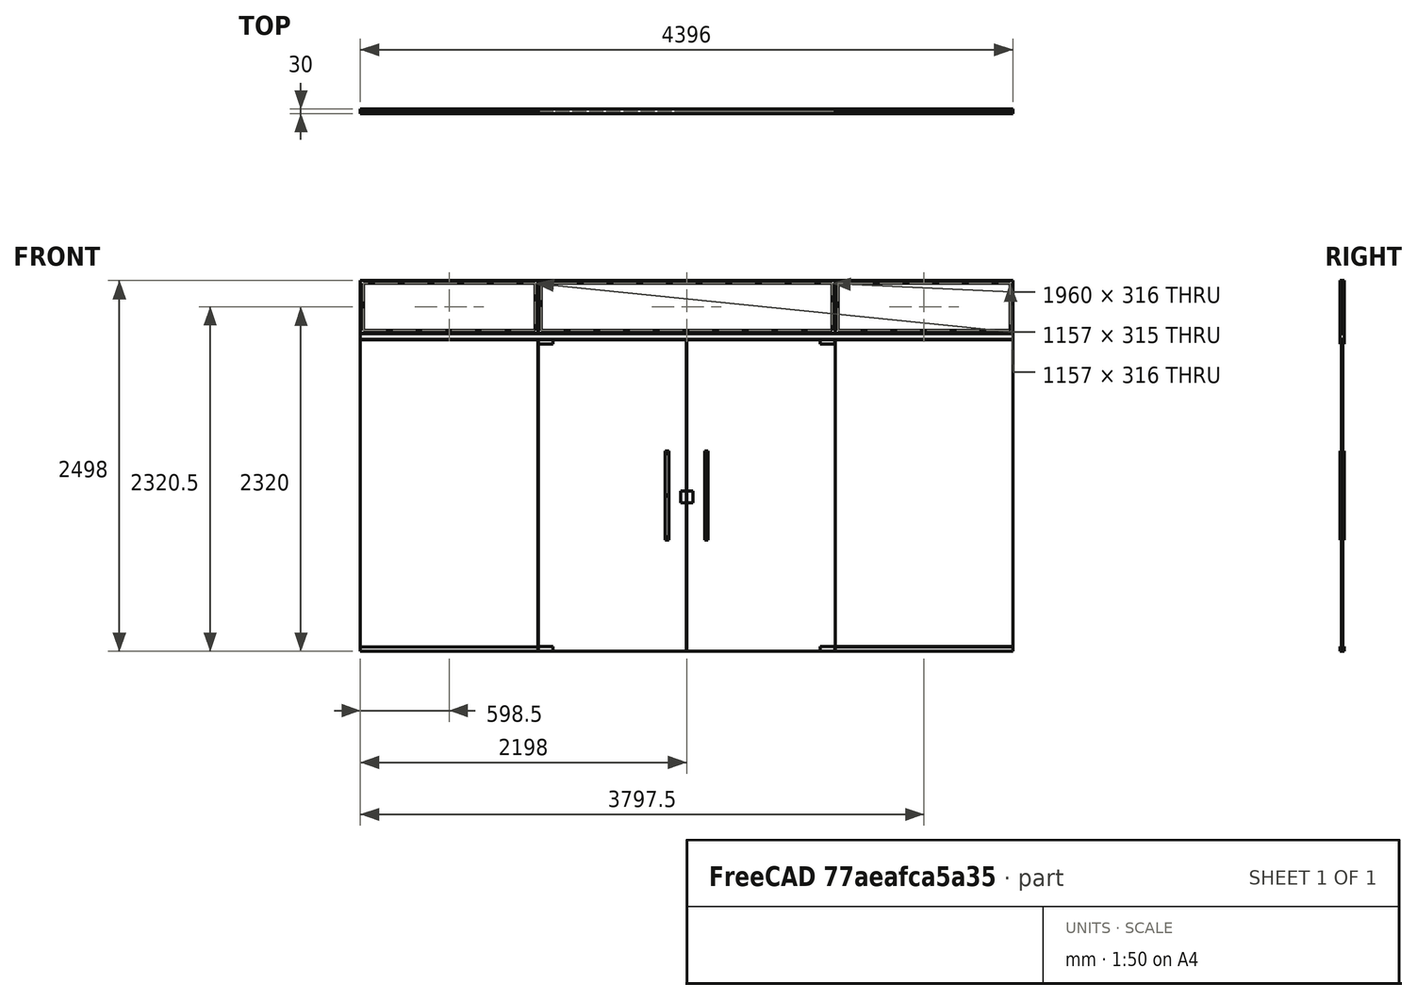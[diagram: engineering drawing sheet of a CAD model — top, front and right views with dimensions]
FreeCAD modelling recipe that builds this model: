
FCSTD DOCUMENT  (FreeCAD 0.16R6704 (Git))
Label: Glass double doors with transom and handles
License: CreativeCommons Attribution
LicenseURL: http://creativecommons.org/licenses/by/4.0/
objects: Sketcher::SketchObject×3, Part::FeaturePython×1, App::DocumentObjectGroup×1
note: 4 computed .brp shape members not serialized (recipe doc carries the construction recipe); baked Part::Feature solids carry a one-line shape summary decoded from their .brp

FEATURE [Sketcher::SketchObject] Sketch138
  Placement = pos=(0,0,0) rot=(1,0,0;1.5708rad)
  sketch-geometry (103):
    g0: LineSegment StartX=1 StartY=0 StartZ=0 EndX=4399 EndY=0 EndZ=0
    g1: LineSegment StartX=4399 StartY=0 StartZ=0 EndX=4399 EndY=2499 EndZ=0
    g2: LineSegment StartX=4399 StartY=2499 StartZ=0 EndX=1 EndY=2499 EndZ=0
    g3: LineSegment StartX=1 StartY=2499 StartZ=0 EndX=1 EndY=0 EndZ=0
    g4: LineSegment StartX=1200 StartY=0 StartZ=0 EndX=2199.5 EndY=0 EndZ=0
    g5: LineSegment StartX=2199.5 StartY=0 StartZ=0 EndX=2199.5 EndY=2100 EndZ=0
    g6: LineSegment StartX=2199.5 StartY=2100 StartZ=0 EndX=1200 EndY=2100 EndZ=0
    g7: LineSegment StartX=1200 StartY=2100 StartZ=0 EndX=1200 EndY=0 EndZ=0
    g8: LineSegment StartX=1201 StartY=2099 StartZ=0 EndX=1301 EndY=2099 EndZ=0
    g9: LineSegment StartX=1301 StartY=2099 StartZ=0 EndX=1301 EndY=2069 EndZ=0
    g10: LineSegment StartX=1301 StartY=2069 StartZ=0 EndX=1201 EndY=2069 EndZ=0
    g11: LineSegment StartX=1201 StartY=2069 StartZ=0 EndX=1201 EndY=2099 EndZ=0
    g12: LineSegment StartX=1201 StartY=1 StartZ=0 EndX=1301 EndY=1 EndZ=0
    g13: LineSegment StartX=1301 StartY=1 StartZ=0 EndX=1301 EndY=31 EndZ=0
    g14: LineSegment StartX=1301 StartY=31 StartZ=0 EndX=1201 EndY=31 EndZ=0
    g15: LineSegment StartX=1201 StartY=31 StartZ=0 EndX=1201 EndY=1 EndZ=0
    g16: LineSegment StartX=2158.5 StartY=1080 StartZ=0 EndX=2198.5 EndY=1080 EndZ=0
    g17: LineSegment StartX=2198.5 StartY=1080 StartZ=0 EndX=2198.5 EndY=1000 EndZ=0
    g18: LineSegment StartX=2198.5 StartY=1000 StartZ=0 EndX=2158.5 EndY=1000 EndZ=0
    g19: LineSegment StartX=2158.5 StartY=1000 StartZ=0 EndX=2158.5 EndY=1080 EndZ=0
    g20: LineSegment StartX=2054.5 StartY=1350 StartZ=0 EndX=2079.5 EndY=1350 EndZ=0
    g21: LineSegment StartX=2079.5 StartY=1350 StartZ=0 EndX=2079.5 EndY=750 EndZ=0
    g22: LineSegment StartX=2079.5 StartY=750 StartZ=0 EndX=2054.5 EndY=750 EndZ=0
    g23: LineSegment StartX=2054.5 StartY=750 StartZ=0 EndX=2054.5 EndY=1350 EndZ=0
    g24: LineSegment [constr] StartX=2067 StartY=1477.64 StartZ=0 EndX=2067 EndY=711 EndZ=0
    g25: Circle CenterX=2067 CenterY=1335 CenterZ=0 NormalX=0 NormalY=0 NormalZ=1 Radius=5
    g26: Circle CenterX=2067 CenterY=1050 CenterZ=0 NormalX=0 NormalY=0 NormalZ=1 Radius=5
    g27: Circle CenterX=2067 CenterY=765 CenterZ=0 NormalX=0 NormalY=0 NormalZ=1 Radius=5
    g28: LineSegment [constr] StartX=712 StartY=1050 StartZ=0 EndX=790 EndY=1050 EndZ=0
    g29: LineSegment StartX=3200 StartY=0 StartZ=0 EndX=2200.5 EndY=0 EndZ=0
    g30: LineSegment StartX=2200.5 StartY=0 StartZ=0 EndX=2200.5 EndY=2100 EndZ=0
    g31: LineSegment StartX=2200.5 StartY=2100 StartZ=0 EndX=3200 EndY=2100 EndZ=0
    g32: LineSegment StartX=3200 StartY=2100 StartZ=0 EndX=3200 EndY=0 EndZ=0
    g33: LineSegment StartX=3199 StartY=2099 StartZ=0 EndX=3099 EndY=2099 EndZ=0
    g34: LineSegment StartX=3099 StartY=2099 StartZ=0 EndX=3099 EndY=2069 EndZ=0
    g35: LineSegment StartX=3099 StartY=2069 StartZ=0 EndX=3199 EndY=2069 EndZ=0
    g36: LineSegment StartX=3199 StartY=2069 StartZ=0 EndX=3199 EndY=2099 EndZ=0
    g37: LineSegment StartX=3199 StartY=1 StartZ=0 EndX=3099 EndY=1 EndZ=0
    g38: LineSegment StartX=3099 StartY=1 StartZ=0 EndX=3099 EndY=31 EndZ=0
    g39: LineSegment StartX=3099 StartY=31 StartZ=0 EndX=3199 EndY=31 EndZ=0
    g40: LineSegment StartX=3199 StartY=31 StartZ=0 EndX=3199 EndY=1 EndZ=0
    g41: LineSegment StartX=2201.5 StartY=1080 StartZ=0 EndX=2241.5 EndY=1080 EndZ=0
    g42: LineSegment StartX=2241.5 StartY=1080 StartZ=0 EndX=2241.5 EndY=1000 EndZ=0
    g43: LineSegment StartX=2241.5 StartY=1000 StartZ=0 EndX=2201.5 EndY=1000 EndZ=0
    g44: LineSegment StartX=2201.5 StartY=1000 StartZ=0 EndX=2201.5 EndY=1080 EndZ=0
    g45: LineSegment StartX=2320.5 StartY=1350 StartZ=0 EndX=2345.5 EndY=1350 EndZ=0
    g46: LineSegment StartX=2345.5 StartY=1350 StartZ=0 EndX=2345.5 EndY=750 EndZ=0
    g47: LineSegment StartX=2345.5 StartY=750 StartZ=0 EndX=2320.5 EndY=750 EndZ=0
    g48: LineSegment StartX=2320.5 StartY=750 StartZ=0 EndX=2320.5 EndY=1350 EndZ=0
    g49: LineSegment [constr] StartX=2333 StartY=1477.64 StartZ=0 EndX=2333 EndY=711 EndZ=0
    g50: Circle CenterX=2333 CenterY=1335 CenterZ=0 NormalX=0 NormalY=0 NormalZ=1 Radius=5
    g51: Circle CenterX=2333 CenterY=1050 CenterZ=0 NormalX=0 NormalY=0 NormalZ=1 Radius=5
    g52: Circle CenterX=2333 CenterY=765 CenterZ=0 NormalX=0 NormalY=0 NormalZ=1 Radius=5
    g53: LineSegment [constr] StartX=1088 StartY=1050 StartZ=0 EndX=1010 EndY=1050 EndZ=0
    g54: LineSegment StartX=0 StartY=2500 StartZ=0 EndX=4400 EndY=2500 EndZ=0
    g55: LineSegment StartX=4400 StartY=2500 StartZ=0 EndX=4400 EndY=0 EndZ=0
    g56: LineSegment StartX=4400 StartY=0 StartZ=0 EndX=0 EndY=0 EndZ=0
    g57: LineSegment StartX=0 StartY=0 StartZ=0 EndX=0 EndY=2500 EndZ=0
    g58: LineSegment StartX=1200 StartY=2498 StartZ=0 EndX=3200 EndY=2498 EndZ=0
    g59: LineSegment StartX=3200 StartY=2498 StartZ=0 EndX=3200 EndY=2142 EndZ=0
    g60: LineSegment StartX=3200 StartY=2142 StartZ=0 EndX=1200 EndY=2142 EndZ=0
    g61: LineSegment StartX=1200 StartY=2142 StartZ=0 EndX=1200 EndY=2498 EndZ=0
    g62: LineSegment StartX=1220 StartY=2478 StartZ=0 EndX=3180 EndY=2478 EndZ=0
    g63: LineSegment StartX=3180 StartY=2478 StartZ=0 EndX=3180 EndY=2162 EndZ=0
    g64: LineSegment StartX=3180 StartY=2162 StartZ=0 EndX=1220 EndY=2162 EndZ=0
    g65: LineSegment StartX=1220 StartY=2162 StartZ=0 EndX=1220 EndY=2478 EndZ=0
    g66: LineSegment StartX=2 StartY=2141 StartZ=0 EndX=4398 EndY=2141 EndZ=0
    g67: LineSegment StartX=4398 StartY=2141 StartZ=0 EndX=4398 EndY=2101 EndZ=0
    g68: LineSegment StartX=4398 StartY=2101 StartZ=0 EndX=2 EndY=2101 EndZ=0
    g69: LineSegment StartX=2 StartY=2101 StartZ=0 EndX=2 EndY=2141 EndZ=0
    g70: LineSegment [constr] StartX=2200 StartY=3422 StartZ=0 EndX=2200 EndY=-753 EndZ=0
    g71: LineSegment StartX=2 StartY=2498 StartZ=0 EndX=1199 EndY=2498 EndZ=0
    g72: LineSegment StartX=1199 StartY=2498 StartZ=0 EndX=1199 EndY=2143 EndZ=0
    g73: LineSegment StartX=1199 StartY=2143 StartZ=0 EndX=2 EndY=2143 EndZ=0
    g74: LineSegment StartX=2 StartY=2143 StartZ=0 EndX=2 EndY=2498 EndZ=0
    g75: LineSegment StartX=22 StartY=2478 StartZ=0 EndX=1179 EndY=2478 EndZ=0
    g76: LineSegment StartX=1179 StartY=2478 StartZ=0 EndX=1179 EndY=2163 EndZ=0
    g77: LineSegment StartX=1179 StartY=2163 StartZ=0 EndX=22 EndY=2163 EndZ=0
    g78: LineSegment StartX=22 StartY=2163 StartZ=0 EndX=22 EndY=2478 EndZ=0
    g79: LineSegment StartX=3201 StartY=2498 StartZ=0 EndX=4398 EndY=2498 EndZ=0
    g80: LineSegment StartX=4398 StartY=2498 StartZ=0 EndX=4398 EndY=2142 EndZ=0
    g81: LineSegment StartX=4398 StartY=2142 StartZ=0 EndX=3201 EndY=2142 EndZ=0
    g82: LineSegment StartX=3201 StartY=2142 StartZ=0 EndX=3201 EndY=2498 EndZ=0
    g83: LineSegment StartX=3221 StartY=2478 StartZ=0 EndX=4378 EndY=2478 EndZ=0
    g84: LineSegment StartX=4378 StartY=2478 StartZ=0 EndX=4378 EndY=2162 EndZ=0
    g85: LineSegment StartX=4378 StartY=2162 StartZ=0 EndX=3221 EndY=2162 EndZ=0
    g86: LineSegment StartX=3221 StartY=2162 StartZ=0 EndX=3221 EndY=2478 EndZ=0
    g87: LineSegment StartX=2 StartY=2100 StartZ=0 EndX=1199 EndY=2100 EndZ=0
    g88: LineSegment StartX=1199 StartY=2100 StartZ=0 EndX=1199 EndY=30 EndZ=0
    g89: LineSegment StartX=1199 StartY=30 StartZ=0 EndX=2 EndY=30 EndZ=0
    g90: LineSegment StartX=2 StartY=30 StartZ=0 EndX=2 EndY=2100 EndZ=0
    g91: LineSegment StartX=3201 StartY=2100 StartZ=0 EndX=4398 EndY=2100 EndZ=0
    g92: LineSegment StartX=4398 StartY=2100 StartZ=0 EndX=4398 EndY=31 EndZ=0
    g93: LineSegment StartX=4398 StartY=31 StartZ=0 EndX=3201 EndY=31 EndZ=0
    g94: LineSegment StartX=3201 StartY=31 StartZ=0 EndX=3201 EndY=2100 EndZ=0
    g95: LineSegment StartX=4398 StartY=30 StartZ=0 EndX=3201 EndY=30 EndZ=0
    g96: LineSegment StartX=3201 StartY=30 StartZ=0 EndX=3201 EndY=0 EndZ=0
    g97: LineSegment StartX=3201 StartY=0 StartZ=0 EndX=4398 EndY=0 EndZ=0
    g98: LineSegment StartX=4398 StartY=0 StartZ=0 EndX=4398 EndY=30 EndZ=0
    g99: LineSegment StartX=2 StartY=29 StartZ=0 EndX=1199 EndY=29 EndZ=0
    g100: LineSegment StartX=1199 StartY=29 StartZ=0 EndX=1199 EndY=0 EndZ=0
    g101: LineSegment StartX=1199 StartY=0 StartZ=0 EndX=2 EndY=0 EndZ=0
    g102: LineSegment StartX=2 StartY=0 StartZ=0 EndX=2 EndY=29 EndZ=0
  constraints (300):
    c: Coincident(g0,g1)
    c: Coincident(g1,g2)
    c: Horizontal(g0)
    c: Horizontal(g2)
    c: Vertical(g1)
    c: Coincident(g4,g5)
    c: Coincident(g5,g6)
    c: Coincident(g6,g7)
    c: Coincident(g7,g4)
    c: Horizontal(g4)
    c: Horizontal(g6)
    c: Vertical(g5)
    c: Vertical(g7)
    c: Coincident(g8,g9)  'Constraint15'
    c: Coincident(g9,g10)
    c: Coincident(g10,g11)
    c: Coincident(g11,g8)
    c: Horizontal(g8)
    c: Horizontal(g10)
    c: Vertical(g9)
    c: Vertical(g11)
    c: Coincident(g12,g13)
    c: Coincident(g13,g14)
    c: Coincident(g14,g15)
    c: Coincident(g15,g12)
    c: Horizontal(g12)
    c: Horizontal(g14)
    c: Vertical(g13)
    c: Vertical(g15)
    c: Coincident(g16,g17)
    c: Coincident(g17,g18)
    c: Coincident(g18,g19)
    c: Coincident(g19,g16)
    c: Horizontal(g16)
    c: Horizontal(g18)
    c: Vertical(g17)
    c: Vertical(g19)
    c: DistanceY(g8,g6) = 1
    c: DistanceX(g6,g8) = 1
    c: DistanceY(g9,g8) = 30  'Altura da dobradiça'
    c: DistanceX(g10,g9) = 100  'Comprimento da dobradiça'
    c: DistanceX(g4,g12) = 1
    c: DistanceY(g4,g12) = 1
    c: DistanceX(g17,g4) = 1
    c: DistanceY(g18,g16) = 80  'Altura da tranca'
    c: DistanceX(g16,g16) = 40  'Largura da tranca'
    c: DistanceY(g4,g18) = 1000
    c: Coincident(g20,g21)
    c: Coincident(g21,g22)
    c: Coincident(g22,g23)
    c: Coincident(g23,g20)
    c: Horizontal(g20)
    c: Horizontal(g22)
    c: Vertical(g21)
    c: Vertical(g23)
    c: DistanceX(g20,g20) = 25  'Largura puxador'
    c: DistanceY(g21,g20) = 600  'Altura do puxador'
    c: Vertical(g24)  'Constraint69'
    c: Symmetric(g20,g20,g24)  'Constraint67'
    c: PointOnObject(g25,g24)  'Constraint72'
    c: PointOnObject(g26,g24)  'Constraint71'
    c: PointOnObject(g27,g24)  'Constraint68'
    c: Radius(g27) = 5  'Apoio puxador'
    c: Equal(g27,g26)  'Constraint83'
    c: Equal(g27,g25)  'Constraint82'
    c: DistanceY(g25,g20) = 15  'Constraint70'
    c: DistanceY(g21,g27) = 15
    c: Horizontal(g28)
    c: PointOnObject(g26,g28)
    c: Symmetric(g22,g20,g28)
    c: DistanceY(g4,g21) = 750  'Distância do puxador ao solo'
    c: DistanceX(g21,g4) = 120  'Distância do puxador'
    c: Coincident(g29,g30)  'Constraint74'
    c: Coincident(g30,g31)
    c: Coincident(g31,g32)
    c: Coincident(g32,g29)
    c: Horizontal(g29)
    c: Horizontal(g31)
    c: Vertical(g30)
    c: Vertical(g32)
    c: Coincident(g33,g34)
    c: Coincident(g34,g35)
    c: Coincident(g35,g36)
    c: Coincident(g36,g33)
    c: Horizontal(g33)
    c: Horizontal(g35)
    c: Vertical(g34)
    c: Vertical(g36)
    c: Coincident(g37,g38)
    c: Coincident(g38,g39)
    c: Coincident(g39,g40)
    c: Coincident(g40,g37)
    c: Horizontal(g37)
    c: Horizontal(g39)
    c: Vertical(g38)
    c: Vertical(g40)
    c: Coincident(g41,g42)
    c: Coincident(g42,g43)
    c: Coincident(g43,g44)
    c: Coincident(g44,g41)
    c: Horizontal(g41)
    c: Horizontal(g43)
    c: Vertical(g42)
    c: Vertical(g44)
    c: Coincident(g45,g46)
    c: Coincident(g46,g47)
    c: Coincident(g47,g48)
    c: Coincident(g48,g45)
    c: Horizontal(g45)
    c: Horizontal(g47)
    c: Vertical(g46)
    c: Vertical(g48)
    c: Vertical(g49)  'Constraint69'
    c: Symmetric(g45,g45,g49)  'Constraint118'
    c: PointOnObject(g50,g49)  'Constraint72'
    c: PointOnObject(g51,g49)  'Constraint119'
    c: PointOnObject(g52,g49)  'Constraint127'
    c: Radius(g52) = 5  'Apoio puxador'
    c: Equal(g52,g51)  'Constraint83'
    c: Equal(g52,g50)  'Constraint82'
    c: Horizontal(g53)  'Constraint123'
    c: PointOnObject(g51,g53)  'Constraint122'
    c: Symmetric(g47,g45,g53)
    c: Coincident(g54,g55)
    c: Coincident(g55,g56)
    c: Coincident(g56,g57)
    c: Coincident(g57,g54)
    c: Horizontal(g54)
    c: Horizontal(g56)
    c: Vertical(g55)
    c: Vertical(g57)
    c: DistanceX(g54,g2) = 1
    c: DistanceY(g2,g54) = 1
    c: DistanceX(g1,g54) = 1
    c: DistanceY(g56,g-1) = 0
    c: DistanceY(g-1,g6) = 2100  'Altura portas'
    c: Coincident(g58,g59)
    c: Coincident(g59,g60)
    c: Coincident(g60,g61)
    c: Coincident(g61,g58)
    c: Horizontal(g58)
    c: Horizontal(g60)
    c: Vertical(g59)
    c: Vertical(g61)
    c: Coincident(g62,g63)
    c: Coincident(g63,g64)
    c: Coincident(g64,g65)
    c: Coincident(g65,g62)
    c: Horizontal(g62)
    c: Horizontal(g64)
    c: Vertical(g63)
    c: Vertical(g65)
    c: Coincident(g66,g67)
    c: Coincident(g67,g68)
    c: Coincident(g68,g69)
    c: Coincident(g69,g66)
    c: Horizontal(g66)
    c: Horizontal(g68)
    c: Vertical(g67)
    c: Vertical(g69)
    c: DistanceY(g66,g60) = 1
    c: DistanceY(g60,g64) = 20
    c: DistanceX(g60,g64) = 20
    c: DistanceY(g62,g58) = 20
    c: DistanceX(g62,g58) = 20
    c: DistanceY(g6,g68) = 1
    c: DistanceY(g68,g66) = 40  'Altura perfil bandeira'
    c: DistanceY(g58,g2) = 1  'Constraint184'
    c: DistanceY(g6,g54) = 400  'Altura bandeira'
    c: Vertical(g3)  'Constraint179'
    c: Coincident(g2,g3)  'Constraint178'
    c: Vertical(g70)
    c: DistanceY(g30,g5) = 0
    c: DistanceX(g5,g30) = 1
    c: Symmetric(g5,g30,g70)
    c: Symmetric(g54,g54,g70)
    c: Symmetric(g24,g49,g70)
    c: DistanceY(g33,g31) = 1
    c: DistanceX(g33,g31) = 1
    c: DistanceY(g29,g37) = 1
    c: DistanceX(g37,g29) = 1
    c: DistanceX(g2,g66) = 1
    c: DistanceX(g66,g1) = 1
    c: DistanceX(g31,g59) = 0
    c: DistanceX(g60,g6) = 0
    c: Equal(g20,g45)
    c: Equal(g16,g41)
    c: Equal(g19,g44)
    c: Symmetric(g16,g41,g70)
    c: DistanceY(g16,g41) = 0
    c: Coincident(g3,g0)
    c: DistanceX(g56,g55) = 4400  'Largura do vão'
    c: Coincident(g71,g72)  'Constraint193'
    c: Coincident(g72,g73)
    c: Coincident(g73,g74)
    c: Coincident(g74,g71)
    c: Horizontal(g71)
    c: Horizontal(g73)
    c: Vertical(g72)
    c: Vertical(g74)
    c: Coincident(g75,g76)
    c: Coincident(g76,g77)
    c: Coincident(g77,g78)
    c: Coincident(g78,g75)
    c: Horizontal(g75)
    c: Horizontal(g77)
    c: Vertical(g76)
    c: Vertical(g78)
    c: Coincident(g79,g80)
    c: Coincident(g80,g81)
    c: Coincident(g81,g82)
    c: Coincident(g82,g79)
    c: Horizontal(g79)
    c: Horizontal(g81)
    c: Vertical(g80)
    c: Vertical(g82)
    c: Coincident(g83,g84)
    c: Coincident(g84,g85)
    c: Coincident(g85,g86)
    c: Coincident(g86,g83)
    c: Horizontal(g83)
    c: Horizontal(g85)
    c: Vertical(g84)
    c: Vertical(g86)
    c: DistanceX(g79,g83) = 20  'Pefil bandeira'
    c: DistanceY(g83,g79) = 20  'Perfil bandeira'
    c: DistanceY(g81,g85) = 20  'Perfil inferior bandeira'
    c: DistanceX(g83,g79) = 20  'Perfil vertical bandeira'
    c: DistanceX(g79,g1) = 1
    c: DistanceY(g79,g1) = 1
    c: DistanceY(g66,g80) = 1
    c: DistanceX(g58,g79) = 1
    c: DistanceX(g71,g58) = 1
    c: DistanceY(g71,g58) = 0
    c: DistanceY(g60,g72) = 1
    c: DistanceX(g71,g75) = 20  'Perfil bandeira 2'
    c: DistanceY(g75,g71) = 20  'Perfil horizontal bandeira 2'
    c: DistanceY(g73,g77) = 20  'Perfil horizontal bandeira 3'
    c: DistanceX(g75,g71) = 20  'Perfil vertical bandeira 4'
    c: DistanceX(g2,g71) = 1
    c: Coincident(g87,g88)
    c: Coincident(g88,g89)
    c: Coincident(g89,g90)
    c: Coincident(g90,g87)
    c: Horizontal(g87)
    c: Horizontal(g89)
    c: Vertical(g88)
    c: Vertical(g90)
    c: Coincident(g91,g92)
    c: Coincident(g92,g93)
    c: Coincident(g93,g94)
    c: Coincident(g94,g91)
    c: Horizontal(g91)
    c: Horizontal(g93)
    c: Vertical(g92)
    c: Vertical(g94)
    c: DistanceX(g68,g87) = 0
    c: DistanceY(g87,g68) = 1
    c: DistanceX(g88,g4) = 1
    c: DistanceY(g91,g31) = 0  'Constraint267'
    c: DistanceX(g31,g91) = 1  'Constraint266'
    c: DistanceX(g91,g67) = 0
    c: DistanceX(g4,g29) = 2000  'Largura das portas'
    c: DistanceY(g56,g0) = 0
    c: DistanceY(g0,g89) = 30  'Altura baquetes inferiores'
    c: DistanceY(g4,g29) = 0
    c: DistanceY(g56,g4) = 0
    c: Coincident(g95,g96)
    c: Coincident(g96,g97)
    c: Coincident(g97,g98)
    c: Coincident(g98,g95)
    c: Horizontal(g95)
    c: Horizontal(g97)
    c: Vertical(g96)
    c: Vertical(g98)
    c: PointOnObject(g96,g0)
    c: DistanceY(g95,g93) = 1
    c: DistanceX(g95,g93) = 0
    c: DistanceX(g95,g92) = 0
    c: DistanceY(g95,g89) = 0
    c: Coincident(g99,g100)
    c: Coincident(g100,g101)
    c: Coincident(g101,g102)
    c: Coincident(g102,g99)
    c: Horizontal(g99)
    c: Horizontal(g101)
    c: Vertical(g100)
    c: Vertical(g102)
    c: DistanceX(g89,g99) = 0
    c: DistanceY(g99,g89) = 1
    c: DistanceY(g0,g101) = 0
    c: DistanceX(g99,g88) = 0
    c: Equal(g9,g34)
    c: Equal(g34,g13)
    c: Equal(g13,g38)
    c: Equal(g10,g14)
    c: Equal(g14,g35)
    c: Equal(g35,g39)
    c: DistanceX(g56) = 0
    c: Symmetric(g6,g31,g70)
FEATURE [Part::FeaturePython] Window096  label="Double glass doors with transom and handles "  # WARN: FeaturePython — macro-defined, semantics opaque (R4)
  Base = -> Sketch138
  Height = 2100
  HoleDepth = 0
  MoveWithHost = true
  Normal = (0,1,0)
  Preset = 6
  Role = 1
  Width = 900
  WindowParts = PORTA 1 | Glass panel | Wire1 | 10.0 | 10.0 | APOIO SUPERIOR PORTA 1 | Frame | Wire2 | 30.0 | 0.0 | APOIO INFERIOR PORTA 1 | Frame | Wire3 | 30.0 | 0.0 | TRANCA 1 | Frame | Wire4 | 30.0 | 0.0 | PUXADOR 1A | Frame | Wire5 | 10.0 | 0.0 | PUXADOR 2A | Frame | Wire13 | 10.0 | 0.0 | APOIO SUPERIOR PUXADOR 1 | Frame | Wire6 | 30.0 | 0.0 | APOIO CENTRAL PUXADOR 1 | Frame | Wire7 | 30.0 | 0.0 | APOIO INFERIOR PUXADOR 1 | Frame | Wire8 | 30.0 | 0.0 | PORTA 2 | Glass panel | Wire9 | 10.0 | 10.0 | APOIOS SUPERIOR PORTA 2 | Frame | Wire10 | 30.0 | 0.0 | APOIO INFERIOR PORTA 2 | Frame | Wire11 | 30.0 | 0.0 | TRANCA 2 | Frame | Wire12 | 30.0 | 0.0 | APOIO SUPERIOR PUXADOR 2 | Frame | Wire14 | 30.0 | 0.0 | APOIO CENTRAL PUXADOR 2 | Frame | Wire15 | 30.0 | 0.0 | APOIO INFERIOR PUXADOR 2 | Frame | Wire16 | 30.0 | 0.0 | PUXADOR 2B | Frame | Wire13 | 10.0 | 20.0 | PERFIL BASE BANDEIRA | Frame | Wire20 | 30.0 | 0.0 | PERFIL BANDEIRA | Frame | Wire19,Wire18 | 30.0 | 0.0 | VIDRO BANDEIRA | Glass panel | Wire19 | 10.0 | 5.0 | VIDRO FIXO 1 | Glass panel | Wire25 | 10.0 | 10.0 | VIDRO FIXO 2 | Glass panel | Wire26 | 10.0 | 10.0 | BAQUETE BANDEIRA 1 | Frame | Wire22,Wire21 | 20.0 | 5.0 | BAQUETE BANDEIRA 2 | Frame | Wire24,Wire23 | 20.0 | 5.0 | VIDRO BANDEIRA 1 | Glass panel | Wire22 | 10.0 | 10.0 | VIDRO BANDEIRA 2 | Glass panel | Wire24 | 10.0 | 5.0 | PUXADOR 1B | Frame | Wire5 | 10.0 | 20.0 | BAGUETE INFERIOR 1 | Frame | Wire28 | 20.0 | 5.0 | BAGUETE INFERIOR 2 | Frame | Wire27 | 20.0 | 5.0
FEATURE [Sketcher::SketchObject] Sketch139  label="Opening indication"
  ExternalGeometry = -> [Window096]
  Placement = pos=(0,10,0) rot=(1,0,0;1.5708rad)
  Support = -> Window096 [Face5]
  sketch-geometry (6):
    g0: LineSegment [constr] StartX=-578.323 StartY=1041.81 StartZ=0 EndX=1784.68 EndY=1041.81 EndZ=0
    g1: LineSegment [constr] StartX=1260 StartY=2272.16 StartZ=0 EndX=1260 EndY=-144.676 EndZ=0
    g2: LineSegment StartX=1200 StartY=1041.81 StartZ=0 EndX=1260 EndY=2100 EndZ=0
    g3: LineSegment StartX=1260 StartY=2100 StartZ=0 EndX=2199.5 EndY=1041.81 EndZ=0
    g4: LineSegment StartX=2199.5 StartY=1041.81 StartZ=0 EndX=1260 EndY=0 EndZ=0
    g5: LineSegment StartX=1260 StartY=0 StartZ=0 EndX=1200 EndY=1041.81 EndZ=0
  constraints (16):
    c: Horizontal(g0)
    c: DistanceY(g-1,g0) = 1041.81  'Altura tranca'
    c: Vertical(g1)
    c: PointOnObject(g2,g0)
    c: Coincident(g2,g3)
    c: PointOnObject(g3,g-5)
    c: Coincident(g3,g4)
    c: PointOnObject(g4,g-6)
    c: Coincident(g4,g5)
    c: Coincident(g5,g2)
    c: PointOnObject(g2,g-4)
    c: PointOnObject(g2,g-3)
    c: PointOnObject(g2,g1)
    c: PointOnObject(g4,g1)
    c: PointOnObject(g3,g0)
    c: DistanceX(g-6,g1) = 60  'Eixo porta'
FEATURE [Sketcher::SketchObject] Sketch140  label="Opening indication "
  ExternalGeometry = -> [Window096]
  Placement = pos=(0,10,0) rot=(1,0,0;1.5708rad)
  Support = -> Window096 [Face50]
  sketch-geometry (6):
    g0: LineSegment [constr] StartX=-496.649 StartY=1041.19 StartZ=0 EndX=2033.7 EndY=1041.19 EndZ=0
    g1: LineSegment [constr] StartX=3140 StartY=2387.2 StartZ=0 EndX=3140 EndY=-146 EndZ=0
    g2: LineSegment StartX=2199.5 StartY=1041.19 StartZ=0 EndX=3140 EndY=0 EndZ=0
    g3: LineSegment StartX=3140 StartY=0 StartZ=0 EndX=3200 EndY=1041.19 EndZ=0
    g4: LineSegment StartX=3200 StartY=1041.19 StartZ=0 EndX=3140 EndY=2100 EndZ=0
    g5: LineSegment StartX=3140 StartY=2100 StartZ=0 EndX=2199.5 EndY=1041.19 EndZ=0
  constraints (16):
    c: Horizontal(g0)
    c: DistanceY(g-1,g0) = 1041.19  'Altura da tranca'
    c: Vertical(g1)
    c: DistanceX(g1,g-6) = 60  'Eixo porta'
    c: PointOnObject(g2,g-4)
    c: PointOnObject(g2,g-6)
    c: Coincident(g2,g3)
    c: PointOnObject(g3,g-5)
    c: Coincident(g3,g4)
    c: PointOnObject(g4,g-3)
    c: Coincident(g4,g5)
    c: Coincident(g5,g2)
    c: PointOnObject(g2,g0)
    c: PointOnObject(g3,g0)
    c: PointOnObject(g2,g1)
    c: PointOnObject(g4,g1)
FEATURE [App::DocumentObjectGroup] Grupo103  label="Double glass doors with transom and handles 001"
  Group = -> [Window096,Sketch139,Sketch140]
